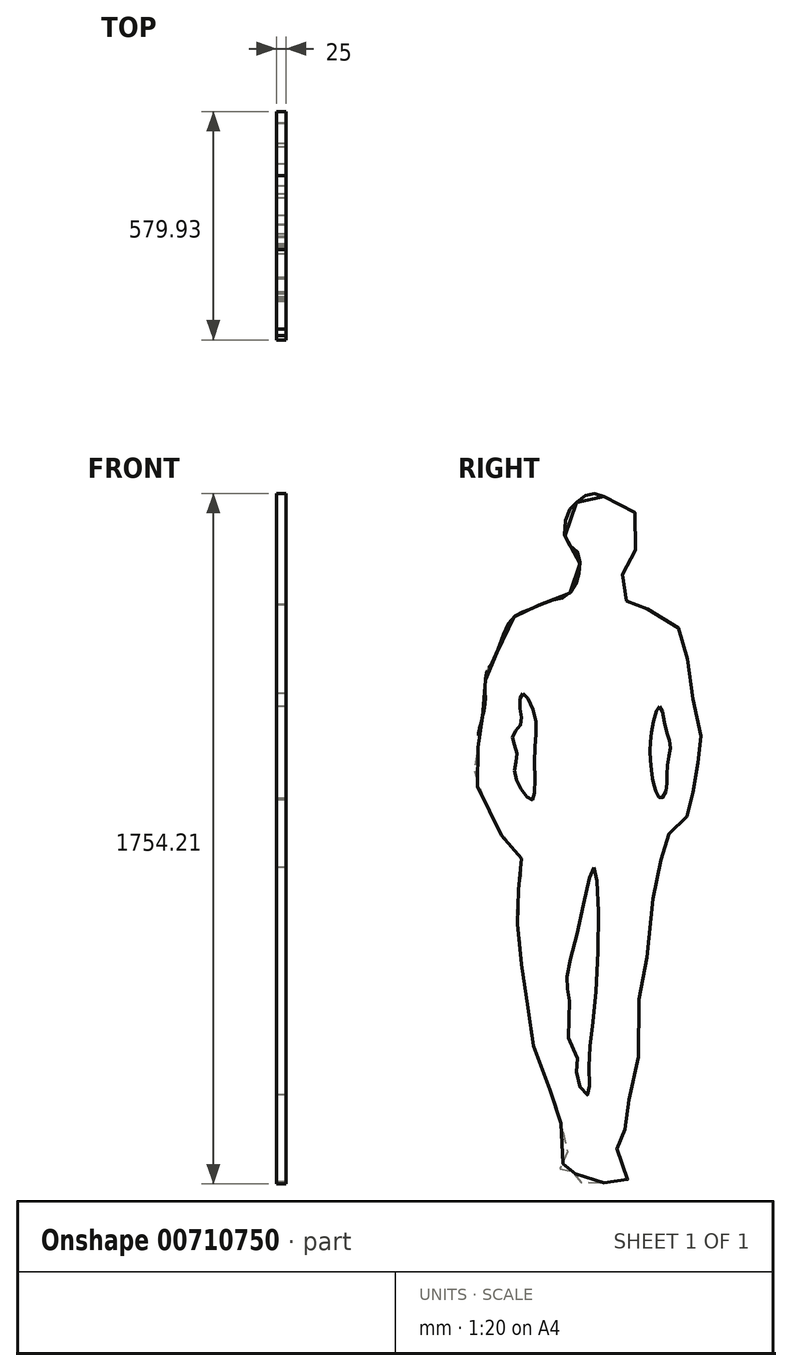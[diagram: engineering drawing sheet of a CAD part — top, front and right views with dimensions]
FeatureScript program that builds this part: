
annotation { "Feature Type Name" : "Feature", "Feature Type Description" : "" }
export const myFeature = defineFeature(function(context is Context, id is Id, definition is map)
    precondition{}
    {
        {
            var Q0;
            Q0=qCreatedBy(makeId("Right.planeOp"), FACE);
            var sketch = newSketch(context, id + "F0", { "sketchPlane" : qUnion([Q0])});
            skLineSegment(sketch, "E0", {"start": v(0, 0) * mm, "end": v(0, 1800) * mm});
            skFitSpline(sketch, "E1", {"points": [v(-67.9, 1762.1) * mm, v(-92.12, 1732.5) * mm, v(-94.81, 1662.56) * mm, v(-65.22, 1632.96) * mm, v(-62.53, 1587.23) * mm, v(-70.6, 1554.94) * mm, v(-100.2, 1519.97) * mm, v(-135.17, 1511.9) * mm, v(-191.66, 1487.69) * mm, v(-207.8, 1482.3) * mm, v(-234.7, 1463.47) * mm, v(-258.92, 1415.05) * mm, v(-288.52, 1345.1) * mm, v(-293.9, 1339.72) * mm, v(-301.97, 1291.3) * mm, v(-301.97, 1248.25) * mm, v(-318.1, 1172.92) * mm, v(-318.1, 1156.77) * mm, v(-323.5, 1113.73) * mm, v(-326.18, 1054.54) * mm, v(-261.61, 922.71) * mm, v(-256.23, 906.57) * mm, v(-218.57, 874.29) * mm, v(-207.8, 836.62) * mm, v(-213.19, 801.65) * mm, v(-221.26, 739.77) * mm, v(-221.26, 704.8) * mm, v(-210.5, 624.09) * mm, v(-207.8, 575.66) * mm, v(-194.35, 489.57) * mm, v(-188.97, 433.07) * mm, v(-172.83, 360.43) * mm, v(-137.86, 271.65) * mm, v(-124.4, 239.37) * mm, v(-105.57, 169.42) * mm, v(-94.81, 96.78) * mm, v(-110.95, 67.19) * mm, v(-97.5, 64.5) * mm, v(-73.29, 56.43) * mm, v(-59.84, 34.9) * mm, v(0, 32.21) * mm, v(50.47, 34.9) * mm, v(61.23, 37.6) * mm, v(34.32, 88.71) * mm, v(34.32, 123.69) * mm, v(39.7, 134.45) * mm, v(50.47, 158.66) * mm, v(58.54, 199.01) * mm, v(63.92, 242.06) * mm, v(85.44, 322.77) * mm, v(88.13, 489.57) * mm, v(104.27, 559.52) * mm, v(120.41, 729.01) * mm, v(139.25, 817.8) * mm, v(150, 885.05) * mm, v(160.77, 911.95) * mm, v(171.53, 925.4) * mm, v(190.36, 946.93) * mm, v(219.96, 973.83) * mm, v(219.96, 1003.42) * mm, v(233.4, 1038.4) * mm, v(236.1, 1076.06) * mm, v(249.55, 1143.32) * mm, v(249.55, 1156.77) * mm, v(238.79, 1207.9) * mm, v(222.65, 1283.22) * mm, v(211.89, 1363.93) * mm, v(206.5, 1404.28) * mm, v(171.53, 1463.47) * mm, v(109.65, 1490.38) * mm, v(69.3, 1501.14) * mm, v(63.92, 1501.14) * mm, v(47.78, 1536.11) * mm, v(42.4, 1568.4) * mm, v(63.92, 1597.99) * mm, v(77.37, 1630.27) * mm, v(88.13, 1697.53) * mm, v(61.23, 1756.72) * mm, v(0, 1775.55) * mm, v(-32.93, 1783.62) * mm, v(-67.9, 1762.1) * mm]});
            skFitSpline(sketch, "E2", {"points": [v(141.94, 1242.86) * mm, v(123.1, 1189.06) * mm, v(117.72, 1124.49) * mm, v(123.1, 1062.61) * mm, v(131.18, 1030.33) * mm, v(144.63, 1008.8) * mm, v(158.08, 1030.33) * mm, v(160.77, 1084.13) * mm, v(168.84, 1140.63) * mm, v(158.08, 1186.37) * mm, v(141.94, 1242.86) * mm]});
            skFitSpline(sketch, "E3", {"points": [v(-205.12, 1275.15) * mm, v(-175.52, 1221.34) * mm, v(-175.52, 1113.73) * mm, v(-180.9, 1006.12) * mm, v(-205.12, 1024.95) * mm, v(-226.64, 1081.44) * mm, v(-221.26, 1127.18) * mm, v(-232.02, 1167.54) * mm, v(-210.5, 1197.13) * mm, v(-213.19, 1242.86) * mm, v(-205.12, 1275.15) * mm]});
            skFitSpline(sketch, "E4", {"points": [v(-24.86, 833.93) * mm, v(-67.9, 667.13) * mm, v(-94.81, 538) * mm, v(-86.74, 492.26) * mm, v(-86.74, 387.34) * mm, v(-67.9, 355.05) * mm, v(-67.9, 295.87) * mm, v(-41, 255.51) * mm, v(-38.31, 317.39) * mm, v(-19.48, 521.85) * mm, v(-24.86, 833.93) * mm]});
            skSolve(sketch);
        }
        {
            var Q0;
            Q0 = qSketchRegion(id + "F0", true);
            extrude(context, id + "F1", {"entities" : qUnion([Q0]), "depth" : 25 * mm, "offsetDistance" : 25 * mm});
        }
    });
